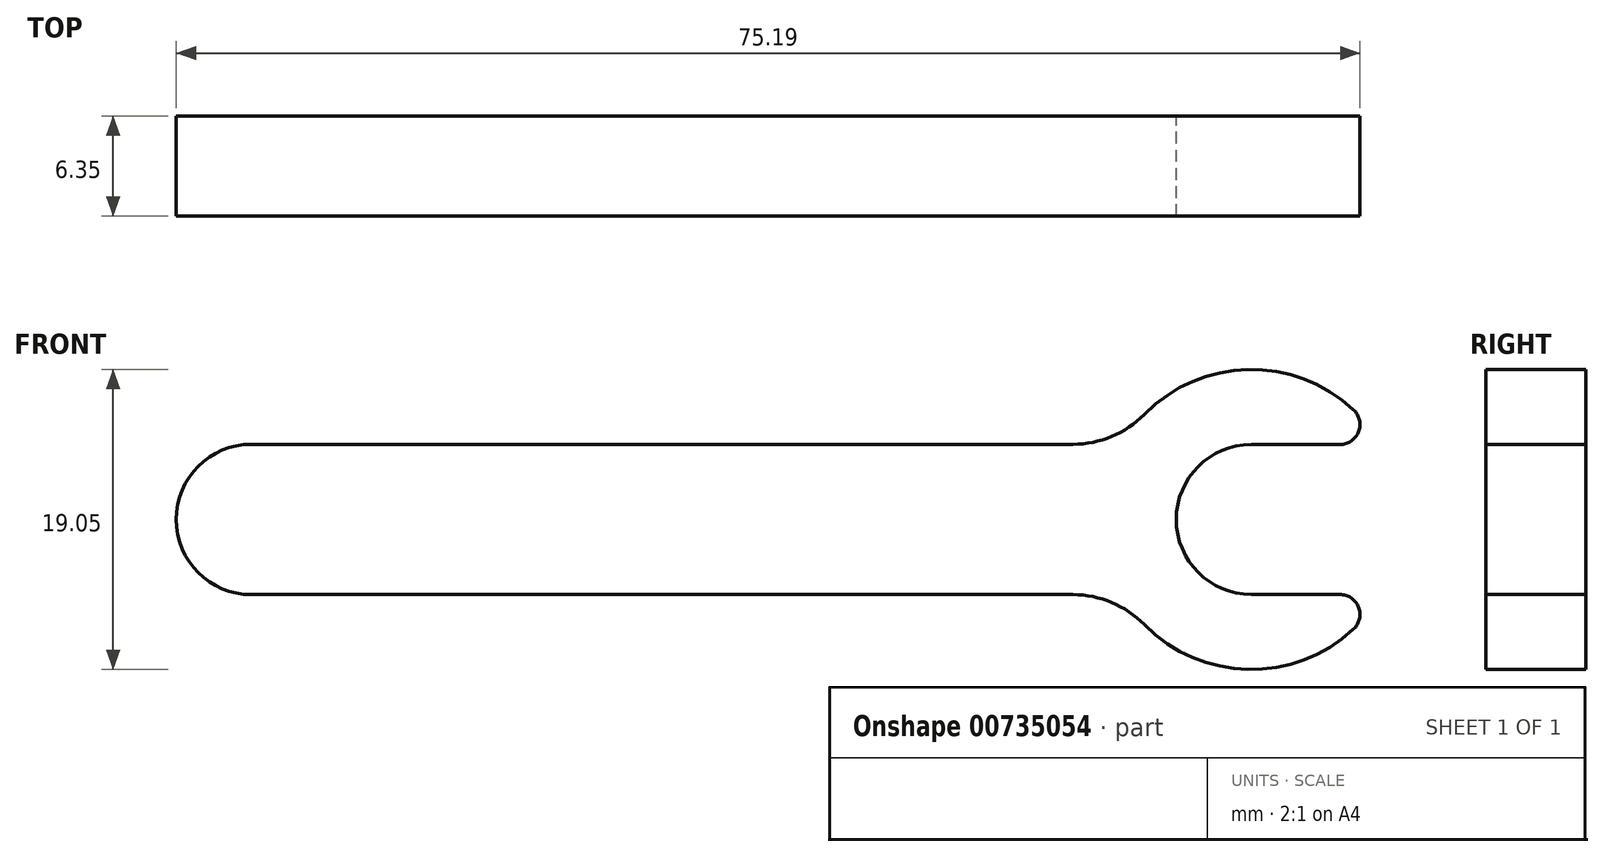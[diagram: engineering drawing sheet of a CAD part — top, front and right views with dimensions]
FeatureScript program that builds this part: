
annotation { "Feature Type Name" : "Feature", "Feature Type Description" : "" }
export const myFeature = defineFeature(function(context is Context, id is Id, definition is map)
    precondition{}
    {
        {
            var Q0;
            Q0=qCreatedBy(makeId("Front.planeOp"),FACE);
            var sketch = newSketch(context, id + "F0", { "sketchPlane" : qUnion([Q0])});
            skLineSegment(sketch, "E0", {"start": v(0, 0) * mm, "end": v(52.18, 0) * mm});
            skLineSegment(sketch, "E1", {"start": v(0, -9.55) * mm, "end": v(52.18, -9.55) * mm});
            skArc(sketch, "E2", {"start": v(0, 0) * mm, "mid": v(-4.78, -4.78) * mm, "end": v(0, -9.55) * mm});
            skArc(sketch, "E3", {"start": v(56.7, -11.45) * mm, "mid": v(54.63, -10.04) * mm, "end": v(52.18, -9.55) * mm});
            skArc(sketch, "E4", {"start": v(52.18, 0) * mm, "mid": v(54.63, 0.5) * mm, "end": v(56.7, 1.9) * mm});
            skLineSegment(sketch, "E5", {"start": v(0, -4.78) * mm, "end": v(121.14, -4.78) * mm, "construction": true});
            skArc(sketch, "E6", {"start": v(70, 2.19) * mm, "mid": v(63.3, 4.75) * mm, "end": v(56.7, 1.9) * mm});
            skArc(sketch, "E7", {"start": v(56.7, -11.45) * mm, "mid": v(63.3, -14.3) * mm, "end": v(70, -11.74) * mm});
            skArc(sketch, "E8", {"start": v(69.14, -0.01) * mm, "mid": v(70.32, 0.8) * mm, "end": v(70, 2.19) * mm});
            skArc(sketch, "E9", {"start": v(70, -11.74) * mm, "mid": v(70.32, -10.34) * mm, "end": v(69.14, -9.54) * mm});
            skLineSegment(sketch, "E10", {"start": v(69.14, -0.01) * mm, "end": v(63.5, -0.01) * mm});
            skLineSegment(sketch, "E11", {"start": v(63.5, -9.54) * mm, "end": v(69.14, -9.54) * mm});
            skArc(sketch, "E12", {"start": v(63.5, -0.01) * mm, "mid": v(58.74, -4.78) * mm, "end": v(63.5, -9.54) * mm});
            skLineSegment(sketch, "E13", {"start": v(63.5, -0.01) * mm, "end": v(63.5, -9.54) * mm, "construction": true});
            skSolve(sketch);
        }
        {
            var Q0;
            Q0 = qSketchRegion(id + "F0", true);
            extrude(context, id + "F1", {"entities" : qUnion([Q0]), "depth" : 6.35 * mm, "offsetDistance" : 25.4 * mm});
        }
    });
